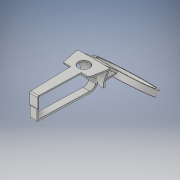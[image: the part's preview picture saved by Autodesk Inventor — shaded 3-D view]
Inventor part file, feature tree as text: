
AUTODESK INVENTOR PART (.ipt)
format: ipt  version: 2017 (Build 210142000, 142)  size: 1,438,720 bytes
history: native  units: mm
features: extrude x10, sketch x10, fillet x8, other x2, plane x1
ambient origin geometry x8: Origin, YZ Plane, XZ Plane, XY Plane, X Axis, Y Axis, Z Axis, Center Point
bodies: Body1 (feature_tree)
feature tree (31):
  extrude  "Extrusion2"  Depth=2.5mm TaperAngle=0.0deg
  extrude  "Extrusion3"  Depth=12.391838mm
  extrude  "Extrusion5"  Depth=28.099801mm
  plane  "Work Plane1"
  extrude  "Extrusion6"  Depth=6.5mm
  extrude  "Extrusion7"  Depth=3.5mm TaperAngle=0.0deg
  extrude  "Extrusion8"  Depth=2.5mm TaperAngle=0.0deg
  extrude  "Extrusion9"  Depth=2.5mm
  extrude  "Extrusion10"  Depth=2.5mm
  extrude  "Extrusion11"  Depth=22.863813mm
  fillet  "Fillet1"  Radius=4.0mm
  fillet  "Fillet3"  Radius=38.0mm
  fillet  "Fillet4"  Radius=10.0mm
  fillet  "Fillet5"  Radius=10.0mm
  fillet  "Fillet6"  Radius=1.4mm
  extrude  "Extrusion13"  Depth=0.45mm
  fillet  "Fillet8"  [1 undecoded]
  fillet  "Fillet9"  Radius=0.45mm
  fillet  "Fillet10"  Radius=2.0mm
  sketch  "sketch1 - front_main"  dims[d66=26.0mm d67=12.391838mm]
  other  "Image1"
  sketch  "sketch2 - bottom_front_tab"  dims[d68=26.0mm d69=28.099801mm]
  sketch  "sketch3 - top_tab"  dims[d70=9.0mm d73=6.5mm]
  other  "Image2"
  sketch  "sketch5 - bottom_hinge"  dims[d74=6.5mm d76=3.5mm d77=0.0mm]
  sketch  "sketch6 - hinge_part"  dims[d82=17.0mm d88=2.5mm d89=0.0mm]
  sketch  "sketch7 - drink_arm"  dims[d90=12.789mm d91=0.0mm d92=2.5mm]
  sketch  "sketch8 - support_arm_arc_hole"  dims[d94=4.6mm d95=2.5mm]
  sketch  "sketch9 - cup_holder"  dims[d96=3.5mm d97=0.0mm d98=22.863813mm d99=4.0mm d100=38.0mm d101=0.0mm d106=10.0mm d107=0.0mm d109=10.0mm d110=0.0mm d111=1.4mm]
  sketch  "Sketch13"  dims[d12=2.5mm d13=0.0mm d18=2.5mm d19=0.0mm]
  sketch  "sketch4 - xbox_hole"  dims[d113=0.4mm d118=20.0mm d119=90.0deg d120=0.45mm d121=2.0mm d122=0.5mm d125=3.0mm d126=0.0mm d128=0.45mm d129=0.45mm d130=4.0mm]
note: 1 required parameter value undecoded (feature->parameter linkage not recoverable at this tier; creation-order binding heuristic only, values carry confidence <= 0.55)
